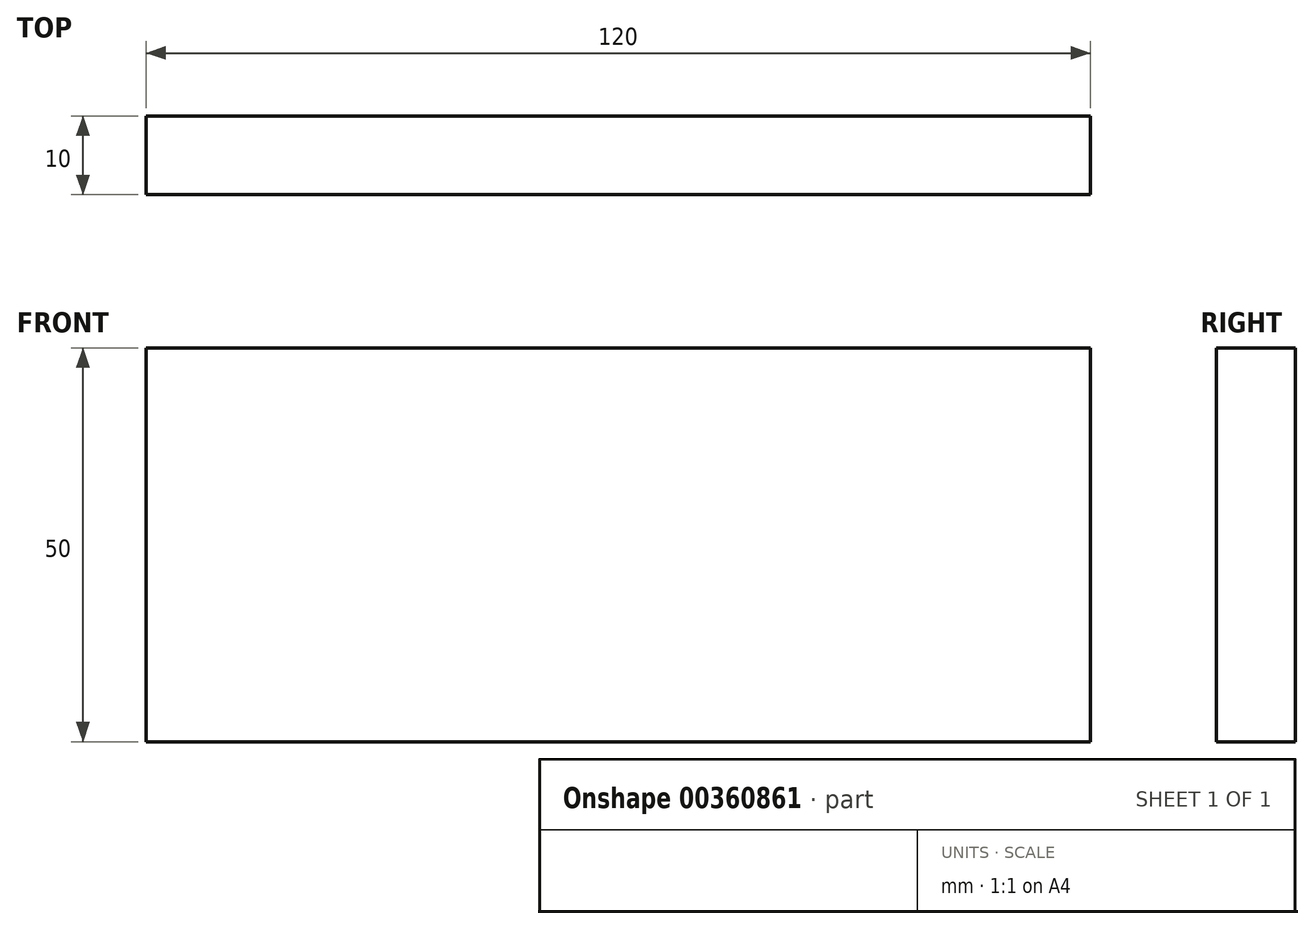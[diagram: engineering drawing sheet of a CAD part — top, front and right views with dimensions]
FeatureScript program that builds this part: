
annotation { "Feature Type Name" : "Feature", "Feature Type Description" : "" }
export const myFeature = defineFeature(function(context is Context, id is Id, definition is map)
    precondition{}
    {
        {
            var Q0;
            Q0=qCreatedBy(makeId("Front.planeOp"),FACE);
            var sketch = newSketch(context, id + "F0", { "sketchPlane" : qUnion([Q0])});
            skLineSegment(sketch, "E0.bottom", {"start": v(60, -25) * mm, "end": v(-60, -25) * mm});
            skLineSegment(sketch, "E0.top", {"start": v(60, 25) * mm, "end": v(-60, 25) * mm});
            skLineSegment(sketch, "E0.left", {"start": v(60, -25) * mm, "end": v(60, 25) * mm});
            skLineSegment(sketch, "E0.right", {"start": v(-60, -25) * mm, "end": v(-60, 25) * mm});
            skPoint(sketch, "E0.middle", {"position": v(0, 0) * mm});
            skSolve(sketch);
        }
        {
            var Q0;
            Q0 = qSketchRegion(id + "F0", true);
            extrude(context, id + "F1", {"entities" : qUnion([Q0]), "depth" : 10 * mm});
        }
    });
